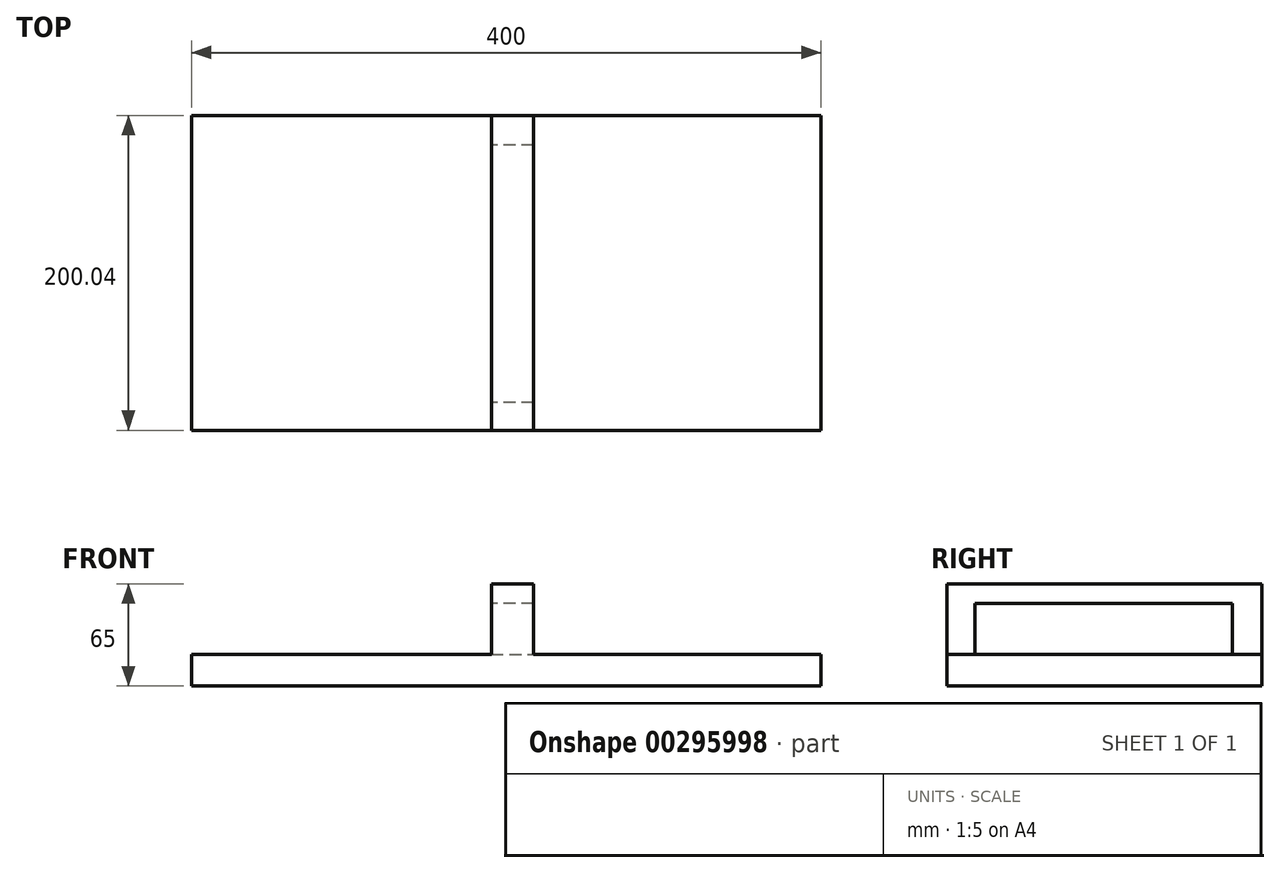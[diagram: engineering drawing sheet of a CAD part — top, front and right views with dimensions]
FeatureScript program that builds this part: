
annotation { "Feature Type Name" : "Feature", "Feature Type Description" : "" }
export const myFeature = defineFeature(function(context is Context, id is Id, definition is map)
    precondition{}
    {
        {
            var Q0;
            Q0=qCreatedBy(makeId("Top.planeOp"),FACE);
            var sketch = newSketch(context, id + "F0", { "sketchPlane" : qUnion([Q0])});
            skLineSegment(sketch, "E0.bottom", {"start": v(0, 0) * mm, "end": v(400, 0) * mm});
            skLineSegment(sketch, "E0.top", {"start": v(0, 200) * mm, "end": v(400, 200) * mm});
            skLineSegment(sketch, "E0.left", {"start": v(0, 0) * mm, "end": v(0, 200) * mm});
            skLineSegment(sketch, "E0.right", {"start": v(400, 0) * mm, "end": v(400, 200) * mm});
            skSolve(sketch);
        }
        {
            var Q0;
            Q0 = qSketchRegion(id + "F0", true);
            extrude(context, id + "F1", {"entities" : qUnion([Q0]), "oppositeDirection" : true, "depth" : 25 * mm});
        }
        {
            var Q0;
            Q0=qCreatedBy(makeId("Top.planeOp"),FACE);
            var sketch = newSketch(context, id + "F2", { "sketchPlane" : qUnion([Q0])});
            skLineSegment(sketch, "E1.bottom", {"start": v(190.59, 200.04) * mm, "end": v(217.36, 200.04) * mm});
            skLineSegment(sketch, "E1.top", {"start": v(190.59, 0) * mm, "end": v(217.36, 0) * mm});
            skLineSegment(sketch, "E1.left", {"start": v(190.59, 200.04) * mm, "end": v(190.59, 0) * mm});
            skLineSegment(sketch, "E1.right", {"start": v(217.36, 200.04) * mm, "end": v(217.36, 0) * mm});
            skSolve(sketch);
        }
        {
            var Q0;
            Q0 = qSketchRegion(id + "F2", true);
            extrude(context, id + "F3", {"entities" : qUnion([Q0]), "operationType" : NewBodyOperationType.ADD, "depth" : 45 * mm});
        }
        {
            var Q0;
            Q0=qCreatedBy(makeId("Right.planeOp"),FACE);
            var sketch = newSketch(context, id + "F4", { "sketchPlane" : qUnion([Q0])});
            skLineSegment(sketch, "E2.bottom", {"start": v(17.7, 32.64) * mm, "end": v(181.22, 32.64) * mm});
            skLineSegment(sketch, "E2.top", {"start": v(17.7, 0) * mm, "end": v(181.22, 0) * mm});
            skLineSegment(sketch, "E2.left", {"start": v(17.7, 32.64) * mm, "end": v(17.7, 0) * mm});
            skLineSegment(sketch, "E2.right", {"start": v(181.22, 32.64) * mm, "end": v(181.22, 0) * mm});
            skSolve(sketch);
        }
        {
            var Q0;
            Q0 = qSketchRegion(id + "F4", true);
            extrude(context, id + "F5", {"entities" : qUnion([Q0]), "operationType" : NewBodyOperationType.REMOVE, "endBound" : BoundingType.THROUGH_ALL, "depth" : 25 * mm});
        }
        {
            var Q0;
            Q0=qCreatedBy(makeId("Top.planeOp"),FACE);
            cPlane(context, id + "F6", {"entities" : qUnion([Q0]), "cplaneType" : CPlaneType.OFFSET, "offset" : 20 * mm, "oppositeDirection" : true, "width" : 150 * mm, "height" : 150 * mm});
        }
        {
            var Q0;
            Q0=qCreatedBy(id+"F6.planeOp",FACE);
            var sketch = newSketch(context, id + "F7", { "sketchPlane" : qUnion([Q0])});
            skEllipse(sketch, "E3", {"center": v(199, 100.86) * mm, "majorRadius": 192.85 * mm, "minorRadius": 91.72 * mm, "majorAxis": v(1, 0)});
            skSolve(sketch);
        }
        {
            var Q0;
            Q0 = qSketchRegion(id + "F7", true);
            extrude(context, id + "F8", {"entities" : qUnion([Q0]), "operationType" : NewBodyOperationType.REMOVE, "oppositeDirection" : true, "depth" : 25 * mm, "hasDraft" : true, "draftAngle" : 60 * degree});
        }
        {
            var Q0;
            Q0=qCreatedBy(id+"F6.planeOp",FACE);
            var sketch = newSketch(context, id + "F9", { "sketchPlane" : qUnion([Q0])});
            skLineSegment(sketch, "E4.bottom", {"start": v(201.89, -10.19) * mm, "end": v(414.82, -10.19) * mm});
            skLineSegment(sketch, "E4.top", {"start": v(201.89, 213.98) * mm, "end": v(414.82, 213.98) * mm});
            skLineSegment(sketch, "E4.left", {"start": v(201.89, -10.19) * mm, "end": v(201.89, 213.98) * mm});
            skLineSegment(sketch, "E4.right", {"start": v(414.82, -10.19) * mm, "end": v(414.82, 213.98) * mm});
            skSolve(sketch);
        }
        {
            var Q0;
            Q0 = qSketchRegion(id + "F9", true);
            extrude(context, id + "F10", {"entities" : qUnion([Q0]), "operationType" : NewBodyOperationType.REMOVE, "oppositeDirection" : true, "depth" : 25 * mm});
        }
        {
            var Q0;
            Q0=qCreatedBy(makeId("Top.planeOp"),FACE);
            cPlane(context, id + "F11", {"entities" : qUnion([Q0]), "cplaneType" : CPlaneType.OFFSET, "offset" : 100 * mm, "width" : 150 * mm, "height" : 150 * mm});
        }
        {
            var Q0;
            Q0=qCreatedBy(id+"F6.planeOp",FACE);
            var sketch = newSketch(context, id + "F12", { "sketchPlane" : qUnion([Q0])});
            skLineSegment(sketch, "E5.bottom", {"start": v(409.02, -7.3) * mm, "end": v(-8.41, -7.3) * mm});
            skLineSegment(sketch, "E5.top", {"start": v(409.02, 209.55) * mm, "end": v(-8.41, 209.55) * mm});
            skLineSegment(sketch, "E5.left", {"start": v(409.02, -7.3) * mm, "end": v(409.02, 209.55) * mm});
            skLineSegment(sketch, "E5.right", {"start": v(-8.41, -7.3) * mm, "end": v(-8.41, 209.55) * mm});
            skSolve(sketch);
        }
        {
            var Q0;
            Q0 = qSketchRegion(id + "F12", true);
            extrude(context, id + "F13", {"entities" : qUnion([Q0]), "operationType" : NewBodyOperationType.REMOVE, "oppositeDirection" : true, "depth" : 25 * mm});
        }
    });
